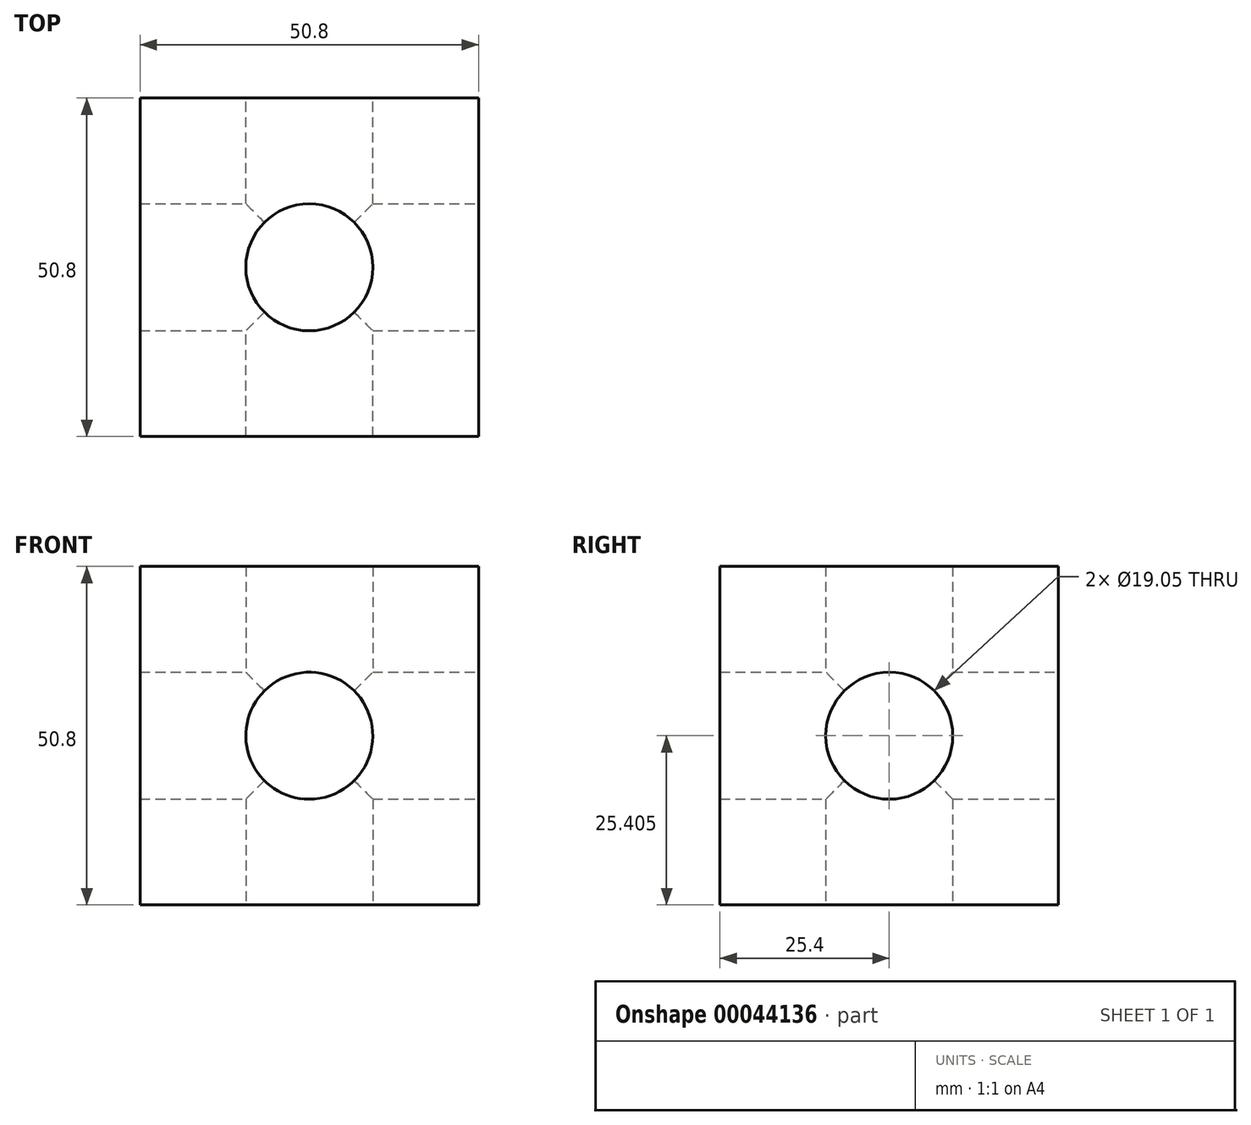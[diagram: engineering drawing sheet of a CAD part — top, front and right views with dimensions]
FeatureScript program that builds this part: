
annotation { "Feature Type Name" : "Feature", "Feature Type Description" : "" }
export const myFeature = defineFeature(function(context is Context, id is Id, definition is map)
    precondition{}
    {
        {
            var Q0;
            Q0=qCreatedBy(makeId("Front.planeOp"),FACE);
            var sketch = newSketch(context, id + "F0", { "sketchPlane" : qUnion([Q0])});
            skLineSegment(sketch, "E0.bottom", {"start": v(-25.4, 20.97) * mm, "end": v(25.4, 20.97) * mm});
            skLineSegment(sketch, "E0.top", {"start": v(-25.4, -29.83) * mm, "end": v(25.4, -29.83) * mm});
            skLineSegment(sketch, "E0.left", {"start": v(-25.4, 20.97) * mm, "end": v(-25.4, -29.83) * mm});
            skLineSegment(sketch, "E0.right", {"start": v(25.4, 20.97) * mm, "end": v(25.4, -29.83) * mm});
            skCircle(sketch, "E1", {"center": v(0, -4.43) * mm, "radius": 9.53 * mm});
            skSolve(sketch);
        }
        {
            var Q0;
            Q0=makeQuery(id+"F0.imprint","IMPRINT",FACE,{"disambiguationData":[TD([[makeQuery(id+"F0.imprint","IMPRINT",EDGE,{"derivedFrom":sQuery(id+"F0.wireOp",EDGE,"E0.bottom")}),-1.0]])]});
            extrude(context, id + "F1", {"entities" : qUnion([Q0]), "depth" : 50.8 * mm});
        }
        {
            var Q0;
            Q0=makeQuery(id+"F1.opExtrude","SWEPT_FACE",FACE,{"disambiguationData":[OSD([sQuery(id+"F0.wireOp",EDGE,"E0.top")])]});
            var sketch = newSketch(context, id + "F2", { "sketchPlane" : qUnion([Q0])});
            skCircle(sketch, "E2", {"center": v(0, 25.4) * mm, "radius": 9.53 * mm});
            skSolve(sketch);
        }
        {
            var Q0;
            Q0=makeQuery(id+"F2.imprint","IMPRINT",FACE,{"disambiguationData":[TD([[makeQuery(id+"F2.imprint","IMPRINT",EDGE,{"derivedFrom":sQuery(id+"F2.wireOp",EDGE,"E2")}),1.0]])]});
            extrude(context, id + "F3", {"entities" : qUnion([Q0]), "operationType" : NewBodyOperationType.REMOVE, "oppositeDirection" : true, "depth" : 50.8 * mm});
        }
        {
            var Q0;
            Q0=makeQuery(id+"F1.opExtrude","SWEPT_FACE",FACE,{"disambiguationData":[OSD([sQuery(id+"F0.wireOp",EDGE,"E0.right")])]});
            var sketch = newSketch(context, id + "F4", { "sketchPlane" : qUnion([Q0])});
            skCircle(sketch, "E3", {"center": v(-25.4, -4.43) * mm, "radius": 9.53 * mm});
            skSolve(sketch);
        }
        {
            var Q0;
            Q0=makeQuery(id+"F4.imprint","IMPRINT",FACE,{"disambiguationData":[TD([[makeQuery(id+"F4.imprint","IMPRINT",EDGE,{"derivedFrom":sQuery(id+"F4.wireOp",EDGE,"E3")}),1.0]])]});
            extrude(context, id + "F5", {"entities" : qUnion([Q0]), "operationType" : NewBodyOperationType.REMOVE, "oppositeDirection" : true, "depth" : 50.8 * mm});
        }
    });
